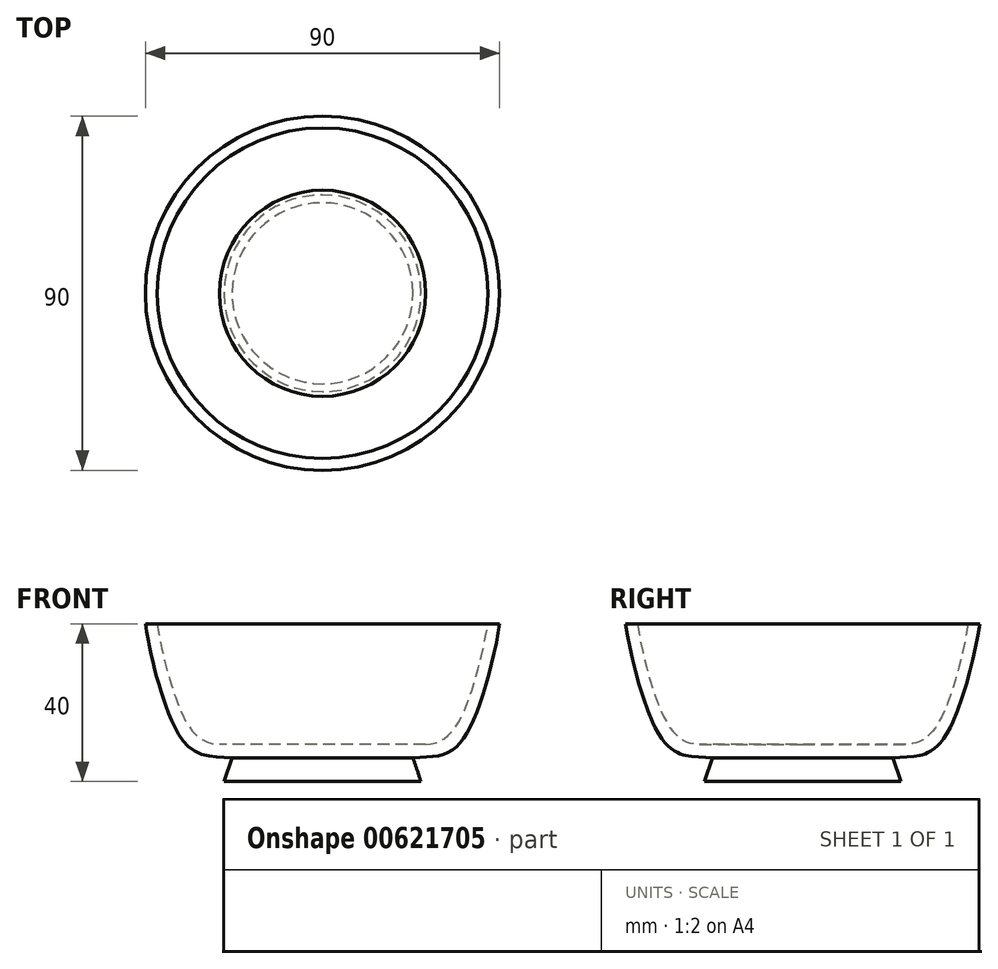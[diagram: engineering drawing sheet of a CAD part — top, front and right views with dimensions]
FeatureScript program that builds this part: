
annotation { "Feature Type Name" : "Feature", "Feature Type Description" : "" }
export const myFeature = defineFeature(function(context is Context, id is Id, definition is map)
    precondition{}
    {
        {
            var Q0;
            Q0=qCreatedBy(makeId("Front.planeOp"),FACE);
            var sketch = newSketch(context, id + "F0", { "sketchPlane" : qUnion([Q0])});
            skLineSegment(sketch, "E0", {"start": v(0, 0) * mm, "end": v(25, 0) * mm});
            skLineSegment(sketch, "E1", {"start": v(25, 0) * mm, "end": v(22.99, 6) * mm});
            skLineSegment(sketch, "E2", {"start": v(0, 40) * mm, "end": v(45, 40) * mm, "construction": true});
            skFitSpline(sketch, "E3", {"points": [v(22.99, 6) * mm, v(30.68, 6.84) * mm, v(34.99, 9.79) * mm, v(39.86, 19.36) * mm, v(45, 40) * mm], "startDerivative": vector(42.77, 1.93) * mm, "endDerivative": vector(7.22, 51.59) * mm});
            skLineSegment(sketch, "E4", {"start": v(45, 40) * mm, "end": v(42, 40) * mm});
            skLineSegment(sketch, "E5", {"start": v(0, 9.4) * mm, "end": v(26.18, 9.4) * mm});
            skFitSpline(sketch, "E6", {"points": [v(26.18, 9.4) * mm, v(32.96, 12.7) * mm, v(38.76, 25.73) * mm, v(42, 40) * mm], "startDerivative": vector(30.7, 0.42) * mm, "endDerivative": vector(5.19, 34.73) * mm});
            skLineSegment(sketch, "E7", {"start": v(0, 9.4) * mm, "end": v(0, 0) * mm});
            skSolve(sketch);
        }
        {
            var Q0;
            Q0 = qSketchRegion(id + "F0", true);
            var Q1;
            Q1=sQuery(id+"F0.wireOp",EDGE,"E7");
            revolve(context, id + "F1", {"entities" : qUnion([Q0]), "axis" : qUnion([Q1]), "revolveType" : RevolveType.FULL});
        }
    });
